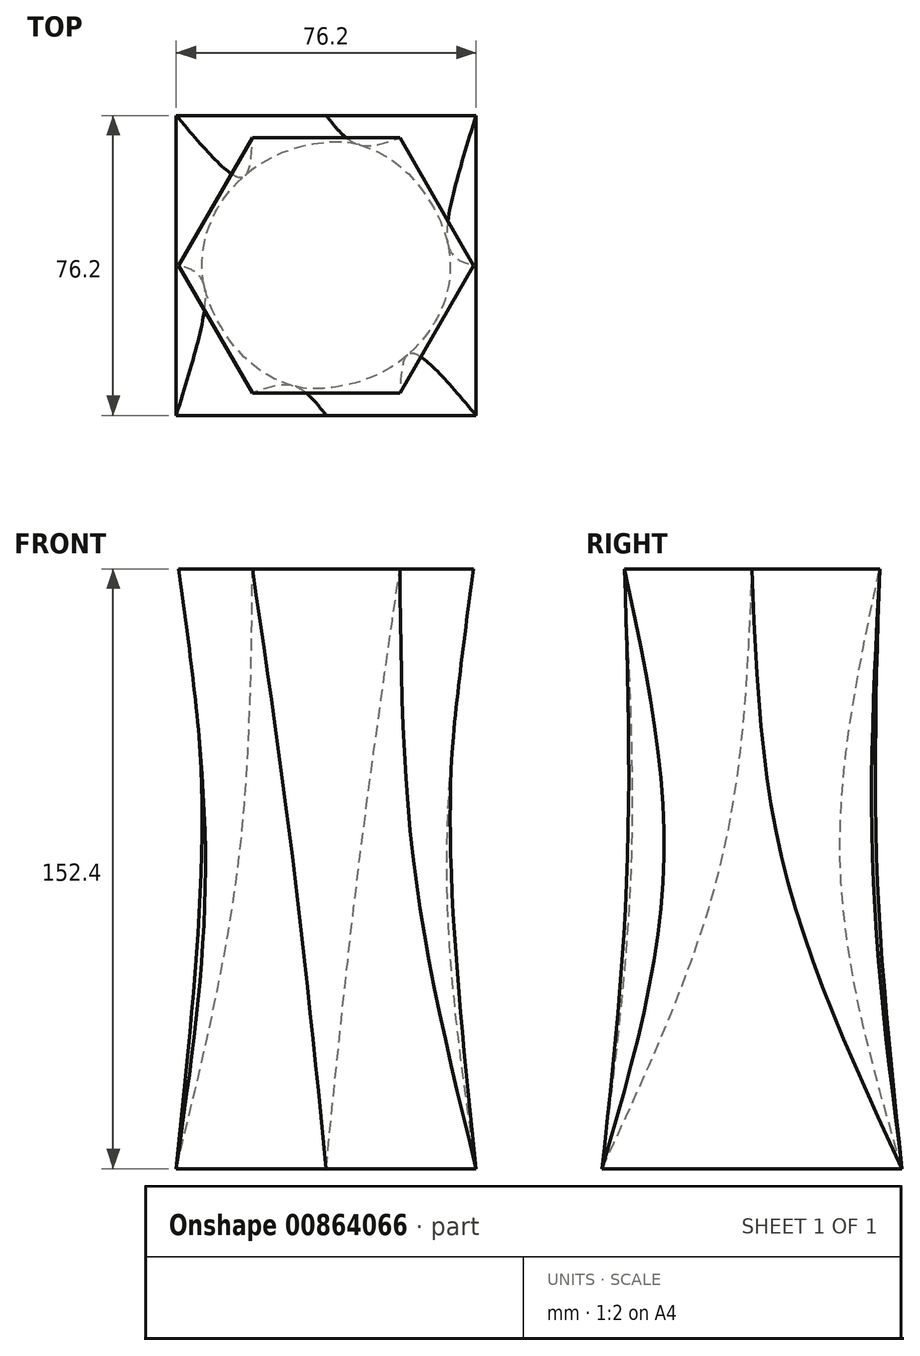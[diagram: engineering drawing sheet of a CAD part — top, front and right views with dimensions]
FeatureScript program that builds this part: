
annotation { "Feature Type Name" : "Feature", "Feature Type Description" : "" }
export const myFeature = defineFeature(function(context is Context, id is Id, definition is map)
    precondition{}
    {
        {
            var Q0;
            Q0=qCreatedBy(makeId("Top.planeOp"),FACE);
            var sketch = newSketch(context, id + "F0", { "sketchPlane" : qUnion([Q0])});
            skLineSegment(sketch, "E0.bottom", {"start": v(-38.1, 38.1) * mm, "end": v(38.1, 38.1) * mm});
            skLineSegment(sketch, "E0.top", {"start": v(-38.1, -38.1) * mm, "end": v(38.1, -38.1) * mm});
            skLineSegment(sketch, "E0.left", {"start": v(-38.1, 38.1) * mm, "end": v(-38.1, -38.1) * mm});
            skLineSegment(sketch, "E0.right", {"start": v(38.1, 38.1) * mm, "end": v(38.1, -38.1) * mm});
            skPoint(sketch, "E0.middle", {"position": v(0, 0) * mm});
            skSolve(sketch);
        }
        {
            var Q0;
            Q0=qCreatedBy(makeId("Top.planeOp"),FACE);
            cPlane(context, id + "F1", {"entities" : qUnion([Q0]), "cplaneType" : CPlaneType.OFFSET, "offset" : 76.2 * mm, "width" : 152.4 * mm, "height" : 152.4 * mm});
        }
        {
            var Q0;
            Q0=qCreatedBy(id+"F1.planeOp",FACE);
            var sketch = newSketch(context, id + "F2", { "sketchPlane" : qUnion([Q0])});
            skCircle(sketch, "E1", {"center": v(0, 0) * mm, "radius": 31.75 * mm});
            skSolve(sketch);
        }
        {
            var Q0;
            Q0=qCreatedBy(id+"F1.planeOp",FACE);
            cPlane(context, id + "F3", {"entities" : qUnion([Q0]), "cplaneType" : CPlaneType.OFFSET, "offset" : 76.2 * mm, "width" : 152.4 * mm, "height" : 152.4 * mm});
        }
        {
            var Q0;
            Q0=qCreatedBy(id+"F3.planeOp",FACE);
            var sketch = newSketch(context, id + "F4", { "sketchPlane" : qUnion([Q0])});
            skCircle(sketch, "E2.cCircle", {"center": v(0, 0) * mm, "radius": 32.43 * mm, "construction": true});
            skLineSegment(sketch, "E2.0", {"start": v(-18.72, 32.43) * mm, "end": v(18.72, 32.43) * mm});
            skLineSegment(sketch, "E2.1", {"start": v(18.72, 32.43) * mm, "end": v(37.45, 0) * mm});
            skLineSegment(sketch, "E2.2", {"start": v(37.45, 0) * mm, "end": v(18.72, -32.43) * mm});
            skLineSegment(sketch, "E2.3", {"start": v(18.72, -32.43) * mm, "end": v(-18.72, -32.43) * mm});
            skLineSegment(sketch, "E2.4", {"start": v(-18.72, -32.43) * mm, "end": v(-37.45, 0) * mm});
            skLineSegment(sketch, "E2.5", {"start": v(-37.45, 0) * mm, "end": v(-18.72, 32.43) * mm});
            skPoint(sketch, "E2.0.midPoint", {"position": v(0, 32.43) * mm});
            skSolve(sketch);
        }
        {
            var Q0;
            Q0=makeQuery(id+"F0.imprint","IMPRINT",FACE,{"disambiguationData":[TD([[makeQuery(id+"F0.imprint","IMPRINT",EDGE,{"derivedFrom":sQuery(id+"F0.wireOp",EDGE,"E0.bottom")}),-1.0]])]});
            var Q1;
            Q1=makeQuery(id+"F2.imprint","IMPRINT",FACE,{"disambiguationData":[TD([[makeQuery(id+"F2.imprint","IMPRINT",EDGE,{"derivedFrom":sQuery(id+"F2.wireOp",EDGE,"E1")}),1.0]])]});
            var Q2;
            Q2=makeQuery(id+"F4.imprint","IMPRINT",FACE,{"disambiguationData":[TD([[makeQuery(id+"F4.imprint","IMPRINT",EDGE,{"derivedFrom":sQuery(id+"F4.wireOp",EDGE,"E2.0")}),-1.0]])]});
            loft(context, id + "F5", {"sheetProfilesArray" : [{ "sheetProfileEntities" : qUnion([Q0]) }, { "sheetProfileEntities" : qUnion([Q1]) }, { "sheetProfileEntities" : qUnion([Q2]) }]});
        }
    });
